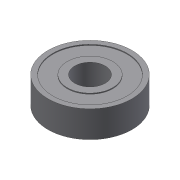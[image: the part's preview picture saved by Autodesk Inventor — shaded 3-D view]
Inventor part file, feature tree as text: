
AUTODESK INVENTOR PART (.ipt)
format: ipt  version: 2017 (Build 210142000, 142)  size: 115,200 bytes
history: native  units: in
note: dims shown in document units (in); Inventor stores cm internally (conversion verified against a paired STEP export)
features: extrude x4, sketch x4, projected_geometry x1
ambient origin geometry x8: Origin, YZ Plane, XZ Plane, XY Plane, X Axis, Y Axis, Z Axis, Center Point
bodies: Solid1 (feature_tree)
feature tree (9):
  extrude  "Extrusion1"  Depth=0.4697in
  extrude  "Extrusion2"  Depth=0.2756in
  extrude  "Extrusion3"  Depth=0.4693in
  extrude  "Extrusion4"  Depth=0.0098in TaperAngle=0.0deg
  sketch  "Sketch1"  dims[d0=0.313in d1=0.4697in]
  sketch  "Sketch2"  dims[d2=0.2756in d3=0.0in d4=0.8661in]
  sketch  "Sketch3"  dims[d5=0.0in d6=0.0in d7=0.4693in]
  sketch  "Sketch4"  dims[d8=0.7657in d9=0.0098in d10=0.0in d11=0.0098in d12=0.0in]
  projected_geometry  "Projected Loop1"
